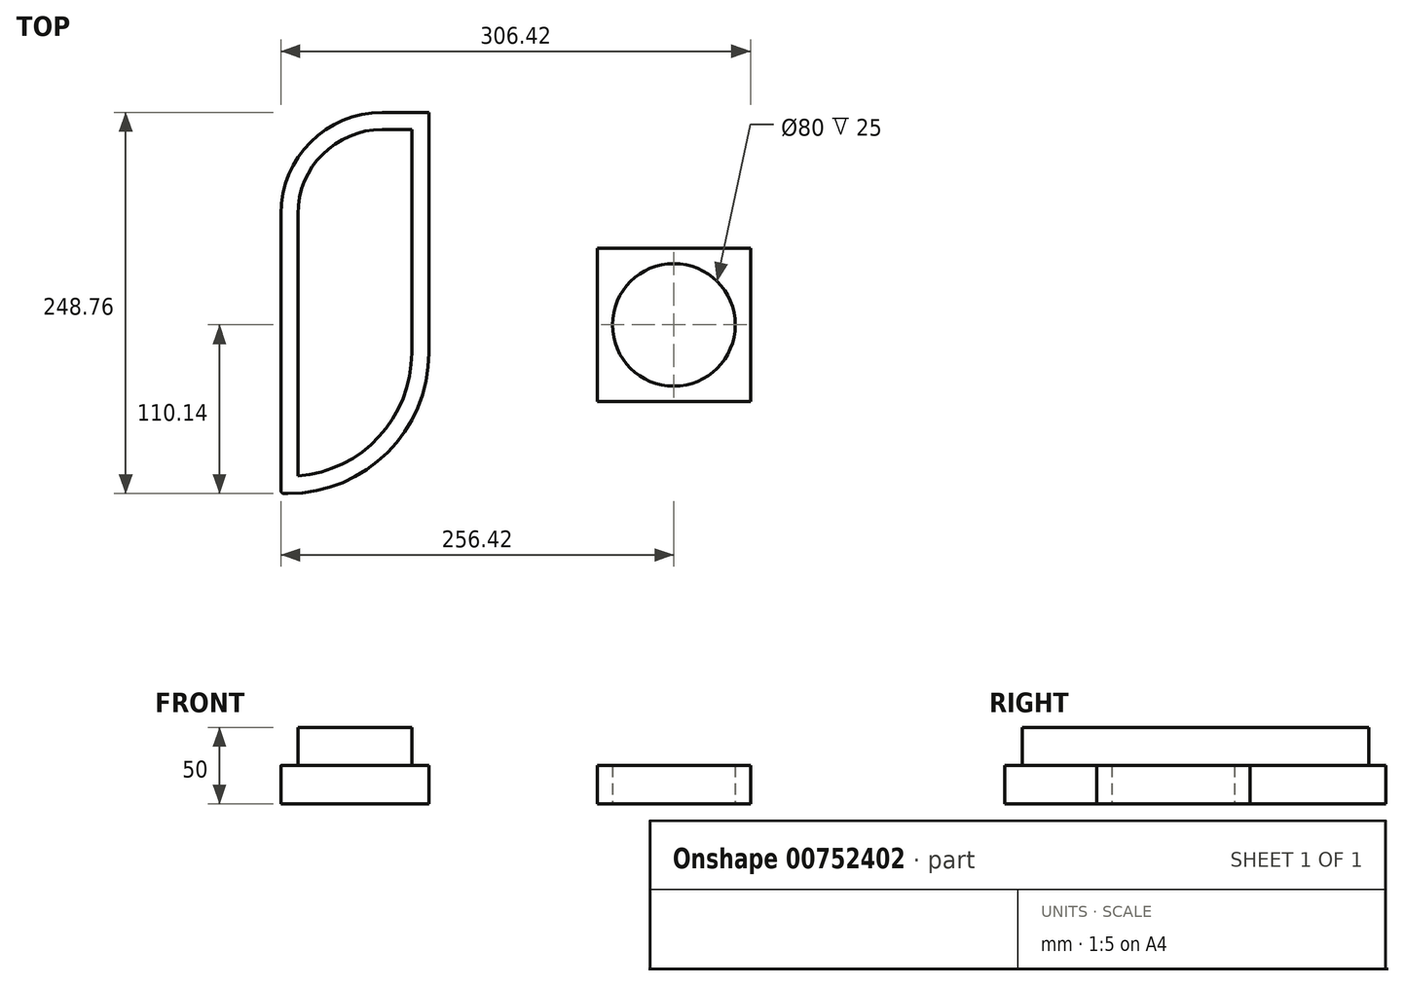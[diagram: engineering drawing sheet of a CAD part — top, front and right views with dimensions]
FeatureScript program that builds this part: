
annotation { "Feature Type Name" : "Feature", "Feature Type Description" : "" }
export const myFeature = defineFeature(function(context is Context, id is Id, definition is map)
    precondition{}
    {
        {
            var Q0;
            Q0=qCreatedBy(makeId("Top.planeOp"),FACE);
            var sketch = newSketch(context, id + "F0", { "sketchPlane" : qUnion([Q0])});
            skLineSegment(sketch, "E0.bottom", {"start": v(-50, -50) * mm, "end": v(50, -50) * mm});
            skLineSegment(sketch, "E0.top", {"start": v(-50, 50) * mm, "end": v(50, 50) * mm});
            skLineSegment(sketch, "E0.left", {"start": v(-50, -50) * mm, "end": v(-50, 50) * mm});
            skLineSegment(sketch, "E0.right", {"start": v(50, -50) * mm, "end": v(50, 50) * mm});
            skPoint(sketch, "E0.middle", {"position": v(0, 0) * mm});
            skLineSegment(sketch, "E1.bottom", {"start": v(-251.75, -110.14) * mm, "end": v(-254.1, -110.14) * mm});
            skLineSegment(sketch, "E1.top", {"start": v(-159.85, 138.62) * mm, "end": v(-190.18, 138.62) * mm});
            skLineSegment(sketch, "E1.left", {"start": v(-159.85, -18.24) * mm, "end": v(-159.85, 138.62) * mm});
            skLineSegment(sketch, "E1.right", {"start": v(-256.42, -107.81) * mm, "end": v(-256.42, 72.39) * mm});
            skPoint(sketch, "E1.middle", {"position": v(-208.13, 14.24) * mm});
            skPoint(sketch, "E2.visualSharp", {"position": v(-256.42, 138.62) * mm});
            skArc(sketch, "E2.filletArc", {"start": v(-190.18, 138.62) * mm, "mid": v(-237.02, 119.22) * mm, "end": v(-256.42, 72.39) * mm});
            skPoint(sketch, "E3.visualSharp", {"position": v(-159.85, -110.14) * mm});
            skArc(sketch, "E3.filletArc", {"start": v(-251.75, -110.14) * mm, "mid": v(-186.76, -83.22) * mm, "end": v(-159.85, -18.24) * mm});
            skPoint(sketch, "E4.visualSharp", {"position": v(-256.42, -110.14) * mm});
            skArc(sketch, "E4.filletArc", {"start": v(-256.42, -107.81) * mm, "mid": v(-255.74, -109.46) * mm, "end": v(-254.1, -110.14) * mm});
            skLineSegment(sketch, "E5.0", {"start": v(-245.28, -98.74) * mm, "end": v(-245.28, 72.39) * mm});
            skArc(sketch, "E5.1", {"start": v(-190.18, 127.48) * mm, "mid": v(-229.14, 111.35) * mm, "end": v(-245.28, 72.39) * mm});
            skArc(sketch, "E5.2", {"start": v(-245.28, -98.74) * mm, "mid": v(-192.4, -73.01) * mm, "end": v(-170.98, -18.24) * mm});
            skLineSegment(sketch, "E5.3", {"start": v(-170.98, -18.24) * mm, "end": v(-170.98, 127.48) * mm});
            skLineSegment(sketch, "E5.4", {"start": v(-170.98, 127.48) * mm, "end": v(-190.18, 127.48) * mm});
            skCircle(sketch, "E6", {"center": v(0, 0) * mm, "radius": 40 * mm});
            skSolve(sketch);
        }
        {
            var Q0;
            Q0=makeQuery(id+"F0.imprint","IMPRINT",FACE,{"disambiguationData":[TD([[makeQuery(id+"F0.imprint","IMPRINT",EDGE,{"derivedFrom":sQuery(id+"F0.wireOp",EDGE,"E5.0")}),-1.0]])]});
            extrude(context, id + "F1", {"entities" : qUnion([Q0]), "depth" : 25 * mm, "offsetDistance" : 25 * mm});
        }
        {
            var Q0;
            Q0 = qSketchRegion(id + "F0", true);
            var Q1;
            Q1=makeQuery(id+"F1.opExtrude","CAP_FACE",FACE,{"disambiguationData":[OSD([sQuery(id+"F0.wireOp",EDGE,"E5.0"),sQuery(id+"F0.wireOp",EDGE,"E5.1"),sQuery(id+"F0.wireOp",EDGE,"E5.2"),sQuery(id+"F0.wireOp",EDGE,"E5.3"),sQuery(id+"F0.wireOp",EDGE,"E5.4")])],"isStart":false});
            extrude(context, id + "F2", {"entities" : qUnion([Q0, Q1]), "operationType" : NewBodyOperationType.ADD, "depth" : 25 * mm, "offsetDistance" : 25 * mm});
        }
    });
